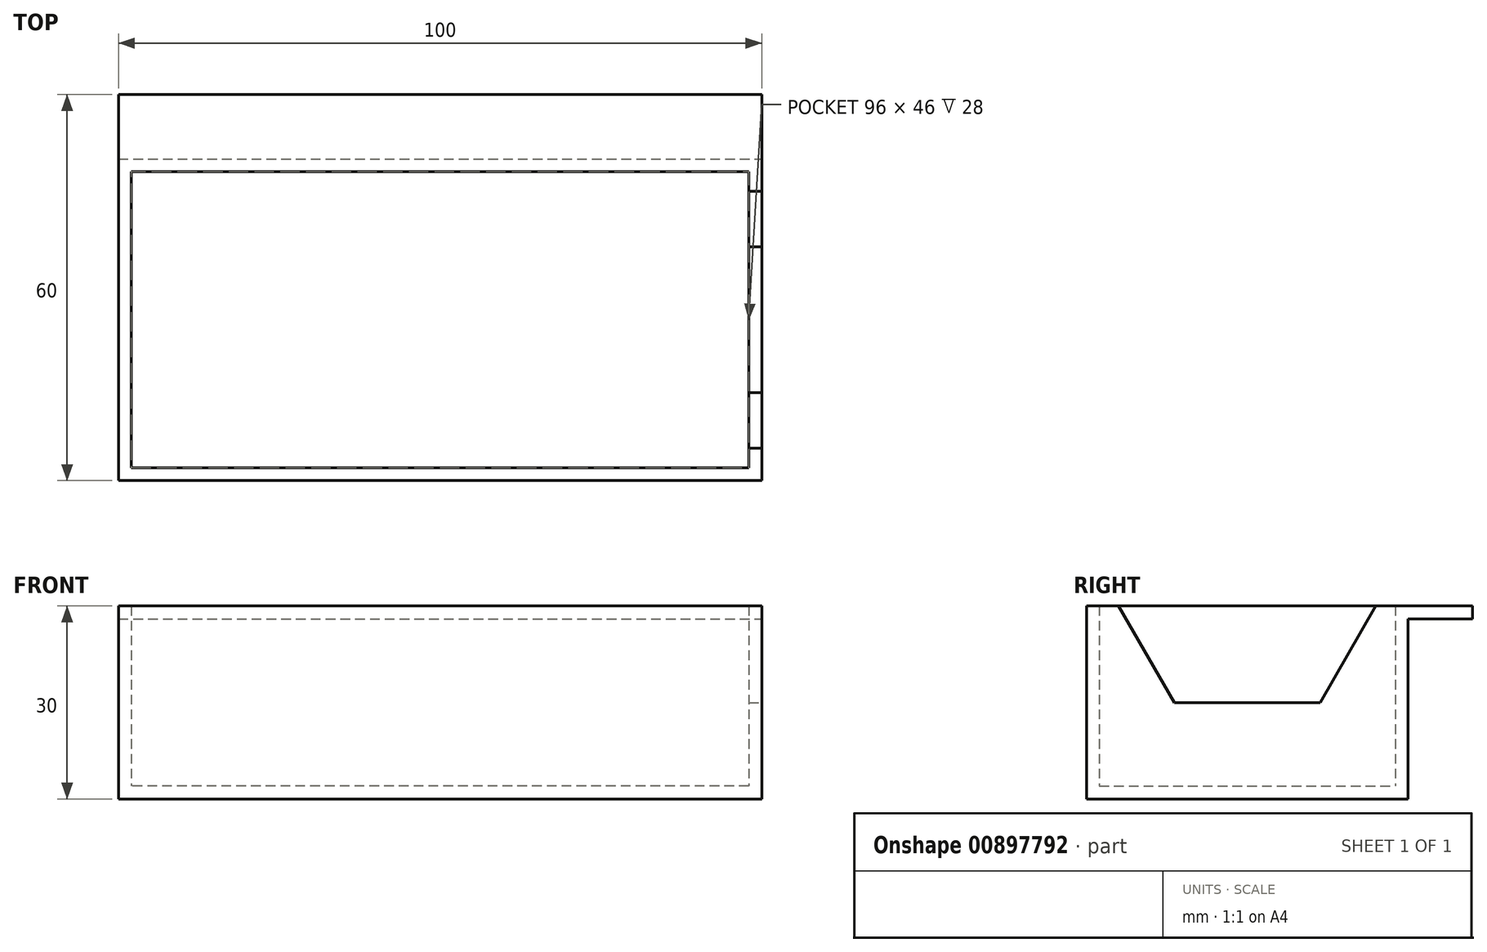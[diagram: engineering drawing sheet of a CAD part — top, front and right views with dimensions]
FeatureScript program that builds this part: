
annotation { "Feature Type Name" : "Feature", "Feature Type Description" : "" }
export const myFeature = defineFeature(function(context is Context, id is Id, definition is map)
    precondition{}
    {
        {
            var Q0;
            Q0=qCreatedBy(makeId("Top.planeOp"),FACE);
            var sketch = newSketch(context, id + "F0", { "sketchPlane" : qUnion([Q0])});
            skLineSegment(sketch, "E0.bottom", {"start": v(50, -25) * mm, "end": v(-50, -25) * mm});
            skLineSegment(sketch, "E0.top", {"start": v(50, 25) * mm, "end": v(-50, 25) * mm});
            skLineSegment(sketch, "E0.left", {"start": v(50, -25) * mm, "end": v(50, 25) * mm});
            skLineSegment(sketch, "E0.right", {"start": v(-50, -25) * mm, "end": v(-50, 25) * mm});
            skPoint(sketch, "E0.middle", {"position": v(0, 0) * mm});
            skSolve(sketch);
        }
        {
            var Q0;
            Q0=qSketchRegion(id+"F0",true);
            extrude(context, id + "F1", {"entities" : qUnion([Q0]), "depth" : 30 * mm, "offsetDistance" : 25 * mm});
        }
        {
            var Q0;
            Q0=makeQuery(id+"F1.opExtrude","CAP_FACE",FACE,{"disambiguationData":[OSD([sQuery(id+"F0.wireOp",EDGE,"E0.bottom"),sQuery(id+"F0.wireOp",EDGE,"E0.top"),sQuery(id+"F0.wireOp",EDGE,"E0.left"),sQuery(id+"F0.wireOp",EDGE,"E0.right")])],"isStart":false});
            shell(context, id + "F2", {"entities" : qUnion([Q0]), "thickness" : 2 * mm});
        }
        {
            var Q0;
            Q0=makeQuery(id+"F1.opExtrude","SWEPT_FACE",FACE,{"disambiguationData":[OSD([sQuery(id+"F0.wireOp",EDGE,"E0.top")])]});
            var sketch = newSketch(context, id + "F3", { "sketchPlane" : qUnion([Q0])});
            skLineSegment(sketch, "E1.bottom", {"start": v(50, 30) * mm, "end": v(-50, 30) * mm});
            skLineSegment(sketch, "E1.top", {"start": v(50, 28) * mm, "end": v(-50, 28) * mm});
            skLineSegment(sketch, "E1.left", {"start": v(50, 30) * mm, "end": v(50, 28) * mm});
            skLineSegment(sketch, "E1.right", {"start": v(-50, 30) * mm, "end": v(-50, 28) * mm});
            skSolve(sketch);
        }
        {
            var Q0;
            Q0=qSketchRegion(id+"F3",true);
            extrude(context, id + "F4", {"entities" : qUnion([Q0]), "operationType" : NewBodyOperationType.ADD, "depth" : 10 * mm, "offsetDistance" : 25 * mm});
        }
        {
            var Q0;
            Q0=makeQuery(id+"F1.opExtrude","SWEPT_FACE",FACE,{"disambiguationData":[OSD([sQuery(id+"F0.wireOp",EDGE,"E0.top")])]});
            var Q1;
            Q1=makeQuery(id+"F1.opExtrude","SWEPT_FACE",FACE,{"disambiguationData":[OSD([sQuery(id+"F0.wireOp",EDGE,"E0.bottom")])]});
            cPlane(context, id + "F5", {"entities" : qUnion([Q0, Q1]), "cplaneType" : CPlaneType.MID_PLANE, "offset" : 85 * mm, "width" : 150 * mm, "height" : 150 * mm});
        }
        {
            var Q0;
            {var subQ0=sQuery(id+"F3.wireOp",EDGE,"E1.right");Q0=makeQuery(id+"FzpPQ3Ug2dkogtD_1.1.F4.boolean.opBoolean","MERGE",FACE,{"derivedFrom":[makeQuery(id+"F4.boolean.opBoolean","MERGE",FACE,{"derivedFrom":[makeQuery(id+"F1.opExtrude","SWEPT_FACE",FACE,{"disambiguationData":[OSD([sQuery(id+"F0.wireOp",EDGE,"E0.left")])]}),makeQuery(id+"F4.opExtrude","SWEPT_FACE",FACE,{"disambiguationData":[OSD([subQ0])]})]}),makeQuery(id+"FzpPQ3Ug2dkogtD_1.1.F4.opExtrude","SWEPT_FACE",FACE,{"disambiguationData":[OSD([subQ0])]})]});}
            var sketch = newSketch(context, id + "F6", { "sketchPlane" : qUnion([Q0])});
            skLineSegment(sketch, "E2", {"start": v(20, 30) * mm, "end": v(11.34, 15) * mm});
            skLineSegment(sketch, "E3", {"start": v(11.34, 15) * mm, "end": v(-11.34, 15) * mm});
            skLineSegment(sketch, "E4", {"start": v(-11.34, 15) * mm, "end": v(-20, 30) * mm});
            skLineSegment(sketch, "E5", {"start": v(-20, 30) * mm, "end": v(20, 30) * mm});
            skLineSegment(sketch, "E6", {"start": v(0, -16.92) * mm, "end": v(0, 44.73) * mm, "construction": true});
            skSolve(sketch);
        }
        {
            var Q0;
            Q0=qSketchRegion(id+"F6",true);
            extrude(context, id + "F7", {"entities" : qUnion([Q0]), "operationType" : NewBodyOperationType.REMOVE, "endBound" : BoundingType.UP_TO_NEXT, "oppositeDirection" : true, "depth" : 25 * mm, "offsetDistance" : 25 * mm});
        }
    });
